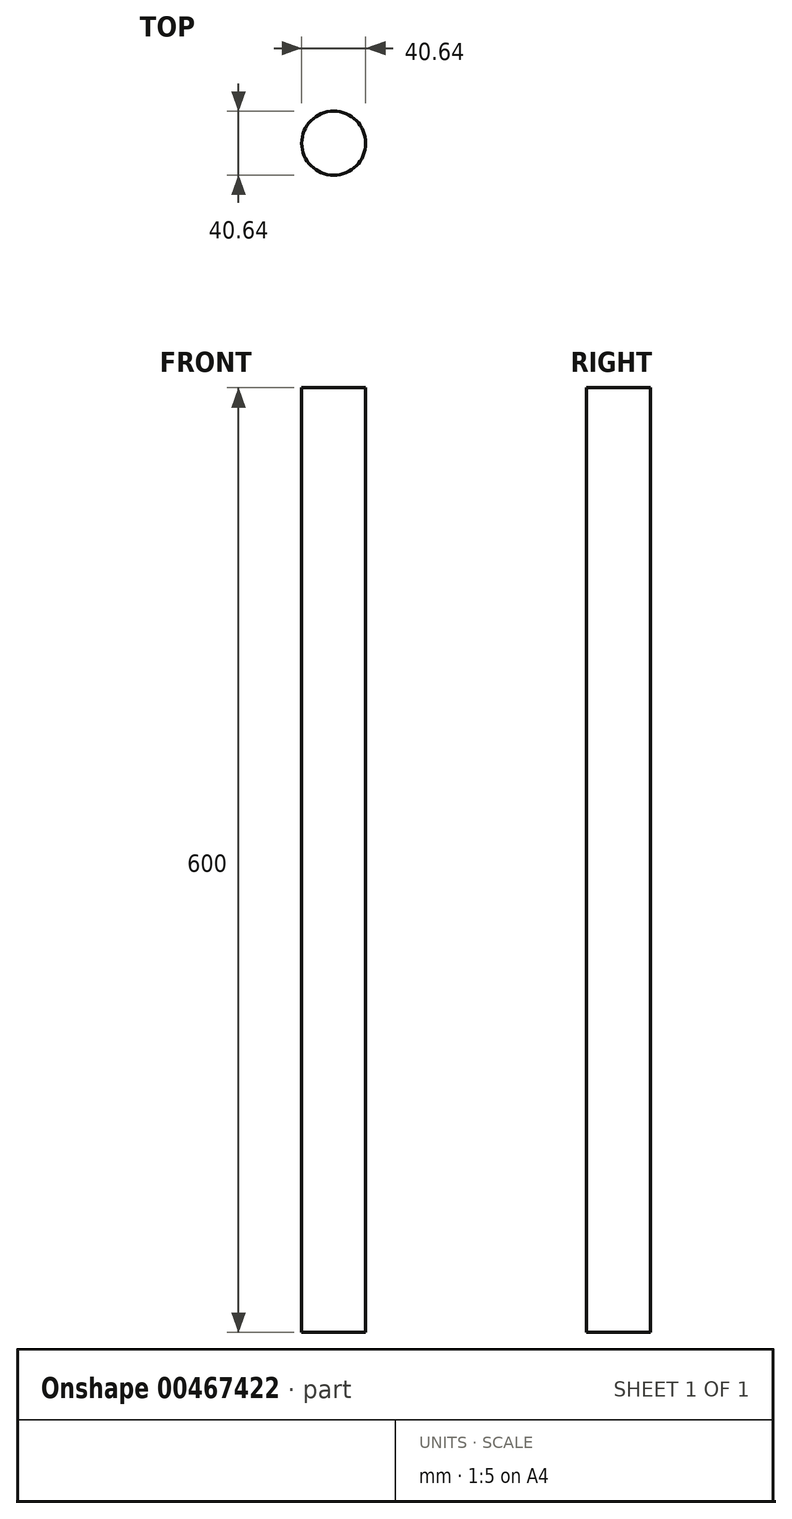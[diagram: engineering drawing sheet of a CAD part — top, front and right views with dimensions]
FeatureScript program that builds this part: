
annotation { "Feature Type Name" : "Feature", "Feature Type Description" : "" }
export const myFeature = defineFeature(function(context is Context, id is Id, definition is map)
    precondition{}
    {
        {
            var Q0;
            Q0=qCreatedBy(makeId("Top.planeOp"),FACE);
            var sketch = newSketch(context, id + "F0", { "sketchPlane" : qUnion([Q0])});
            skCircle(sketch, "E0", {"center": v(-47.18, 30.38) * mm, "radius": 20.32 * mm});
            skSolve(sketch);
        }
        {
            var Q0;
            Q0=makeQuery(id+"F0.imprint","IMPRINT",FACE,{"disambiguationData":[TD([[makeQuery(id+"F0.imprint","IMPRINT",EDGE,{"derivedFrom":sQuery(id+"F0.wireOp",EDGE,"E0")}),1.0]])]});
            extrude(context, id + "F1", {"entities" : qUnion([Q0]), "depth" : 600 * mm});
        }
    });
